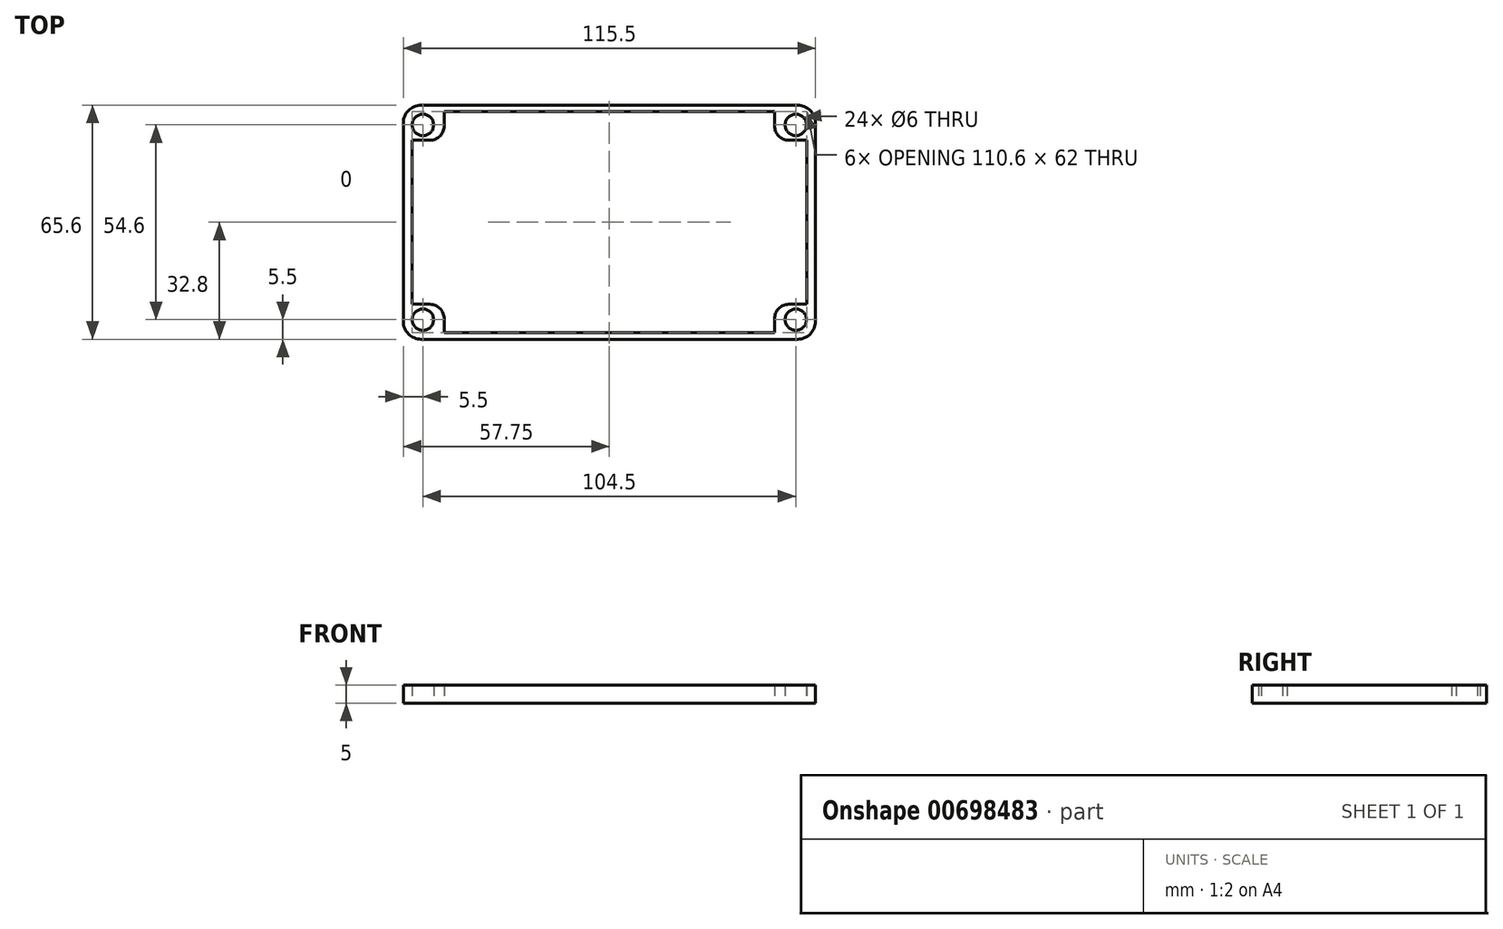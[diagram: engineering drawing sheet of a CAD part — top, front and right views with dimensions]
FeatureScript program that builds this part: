
annotation { "Feature Type Name" : "Feature", "Feature Type Description" : "" }
export const myFeature = defineFeature(function(context is Context, id is Id, definition is map)
    precondition{}
    {
        {
            var Q0;
            Q0=qCreatedBy(makeId("Top.planeOp"),FACE);
            var sketch = newSketch(context, id + "F0", { "sketchPlane" : qUnion([Q0])});
            skLineSegment(sketch, "E0.bottom", {"start": v(52.75, -32.8) * mm, "end": v(-52.75, -32.8) * mm});
            skLineSegment(sketch, "E0.top", {"start": v(52.75, 32.8) * mm, "end": v(-52.75, 32.8) * mm});
            skLineSegment(sketch, "E0.left", {"start": v(57.75, -27.8) * mm, "end": v(57.75, 27.8) * mm});
            skLineSegment(sketch, "E0.right", {"start": v(-57.75, -27.8) * mm, "end": v(-57.75, 27.8) * mm});
            skPoint(sketch, "E0.middle", {"position": v(0, 0) * mm});
            skPoint(sketch, "E1.visualSharp", {"position": v(-57.75, 32.8) * mm});
            skArc(sketch, "E1.filletArc", {"start": v(-52.75, 32.8) * mm, "mid": v(-56.29, 31.34) * mm, "end": v(-57.75, 27.8) * mm});
            skPoint(sketch, "E2.visualSharp", {"position": v(57.75, 32.8) * mm});
            skArc(sketch, "E2.filletArc", {"start": v(57.75, 27.8) * mm, "mid": v(56.29, 31.34) * mm, "end": v(52.75, 32.8) * mm});
            skPoint(sketch, "E3.visualSharp", {"position": v(-57.75, -32.8) * mm});
            skArc(sketch, "E3.filletArc", {"start": v(-57.75, -27.8) * mm, "mid": v(-56.29, -31.34) * mm, "end": v(-52.75, -32.8) * mm});
            skPoint(sketch, "E4.visualSharp", {"position": v(57.75, -32.8) * mm});
            skArc(sketch, "E4.filletArc", {"start": v(52.75, -32.8) * mm, "mid": v(56.29, -31.34) * mm, "end": v(57.75, -27.8) * mm});
            skLineSegment(sketch, "E5.3", {"start": v(46.3, 31) * mm, "end": v(-46.3, 31) * mm});
            skLineSegment(sketch, "E5.4", {"start": v(46.3, -31) * mm, "end": v(-46.3, -31) * mm});
            skLineSegment(sketch, "E6.top", {"start": v(-55.3, 23) * mm, "end": v(-50.3, 23) * mm});
            skLineSegment(sketch, "E6.right", {"start": v(-46.3, 31) * mm, "end": v(-46.3, 27) * mm});
            skPoint(sketch, "E7.orphan", {"position": v(-55, 31) * mm});
            skPoint(sketch, "E8.visualSharp", {"position": v(-46.3, 23) * mm});
            skArc(sketch, "E8.filletArc", {"start": v(-50.3, 23) * mm, "mid": v(-47.47, 24.17) * mm, "end": v(-46.3, 27) * mm});
            skPoint(sketch, "E9.orphan", {"position": v(-55, 27.75) * mm});
            skPoint(sketch, "E10.orphan", {"position": v(-51.75, 31) * mm});
            skLineSegment(sketch, "E11.MirrorCS", {"start": v(-55.3, -23) * mm, "end": v(-50.3, -23) * mm});
            skArc(sketch, "E12.MirrorCS", {"start": v(-50.3, -23) * mm, "mid": v(-47.47, -24.17) * mm, "end": v(-46.3, -27) * mm});
            skLineSegment(sketch, "E13.MirrorCS", {"start": v(-46.3, -31) * mm, "end": v(-46.3, -27) * mm});
            skCircle(sketch, "E14", {"center": v(-52.25, 27.3) * mm, "radius": 3 * mm});
            skCircle(sketch, "E15.MirrorC", {"center": v(-52.25, -27.3) * mm, "radius": 3 * mm});
            skCircle(sketch, "E16.MirrorC", {"center": v(52.25, 27.3) * mm, "radius": 3 * mm});
            skLineSegment(sketch, "E17.MirrorCS", {"start": v(46.3, 31) * mm, "end": v(46.3, 27) * mm});
            skArc(sketch, "E18.MirrorCS", {"start": v(50.3, 23) * mm, "mid": v(47.47, 24.17) * mm, "end": v(46.3, 27) * mm});
            skLineSegment(sketch, "E19.MirrorCS", {"start": v(55.3, 23) * mm, "end": v(50.3, 23) * mm});
            skArc(sketch, "E20.MirrorCS", {"start": v(50.3, -23) * mm, "mid": v(47.47, -24.17) * mm, "end": v(46.3, -27) * mm});
            skLineSegment(sketch, "E21.MirrorCS", {"start": v(55.3, -23) * mm, "end": v(50.3, -23) * mm});
            skLineSegment(sketch, "E22.MirrorCS", {"start": v(46.3, -31) * mm, "end": v(46.3, -27) * mm});
            skCircle(sketch, "E23.MirrorC", {"center": v(52.25, -27.3) * mm, "radius": 3 * mm});
            skLineSegment(sketch, "E24.trimOffspring", {"start": v(-55.3, -23) * mm, "end": v(-55.3, 23) * mm});
            skLineSegment(sketch, "E25.trimOffspring", {"start": v(55.3, -23) * mm, "end": v(55.3, 23) * mm});
            skSolve(sketch);
        }
        {
            var Q0;
            Q0=makeQuery(id+"F0.imprint","IMPRINT",FACE,{"disambiguationData":[TD([[makeQuery(id+"F0.imprint","IMPRINT",EDGE,{"derivedFrom":sQuery(id+"F0.wireOp",EDGE,"E0.bottom")}),-1.0]])]});
            extrude(context, id + "F1", {"entities" : qUnion([Q0]), "depth" : 5 * mm, "offsetDistance" : 25 * mm});
        }
    });
